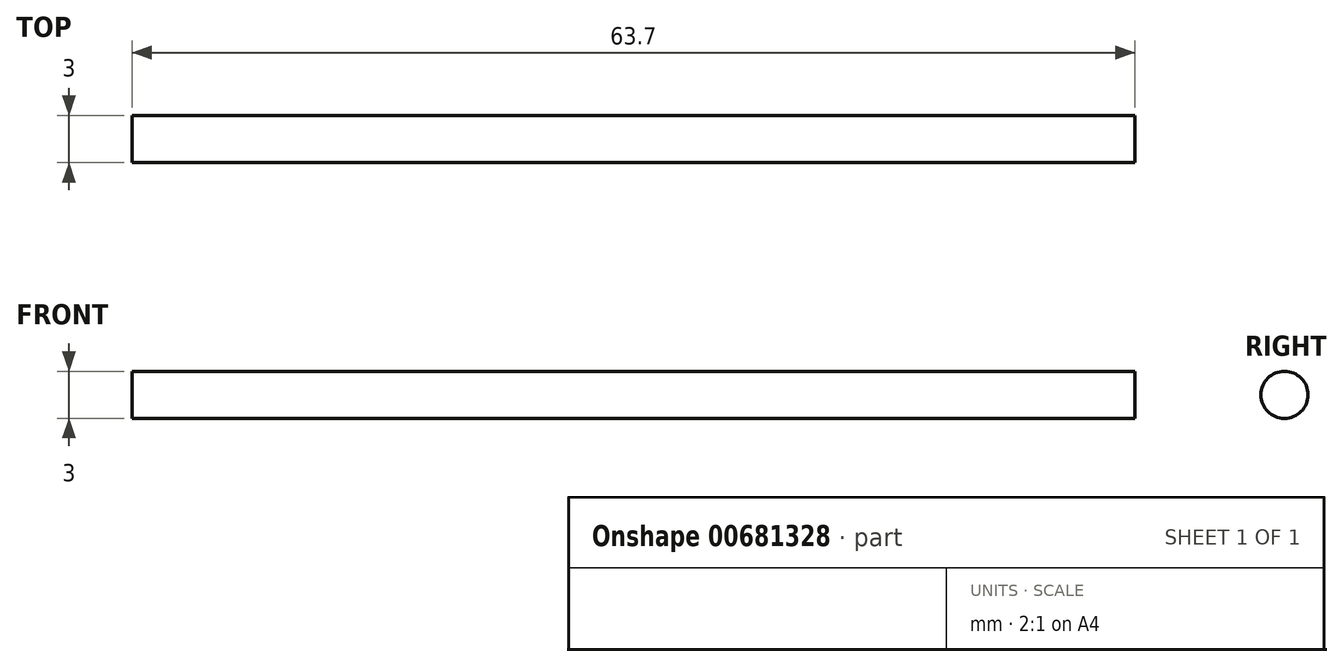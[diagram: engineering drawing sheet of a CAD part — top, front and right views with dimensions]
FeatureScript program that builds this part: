
annotation { "Feature Type Name" : "Feature", "Feature Type Description" : "" }
export const myFeature = defineFeature(function(context is Context, id is Id, definition is map)
    precondition{}
    {
        {
            var Q0;
            Q0=qCreatedBy(makeId("Right.planeOp"),FACE);
            var sketch = newSketch(context, id + "F0", { "sketchPlane" : qUnion([Q0])});
            skCircle(sketch, "E0", {"center": v(0, 0) * mm, "radius": 1.5 * mm});
            skSolve(sketch);
        }
        {
            var Q0;
            Q0=makeQuery(id+"F0.imprint","IMPRINT",FACE,{"disambiguationData":[TD([[makeQuery(id+"F0.imprint","IMPRINT",EDGE,{"derivedFrom":sQuery(id+"F0.wireOp",EDGE,"E0")}),1.0]])]});
            extrude(context, id + "F1", {"entities" : qUnion([Q0]), "depth" : 63.7 * mm, "offsetDistance" : 25.4 * mm});
        }
    });
